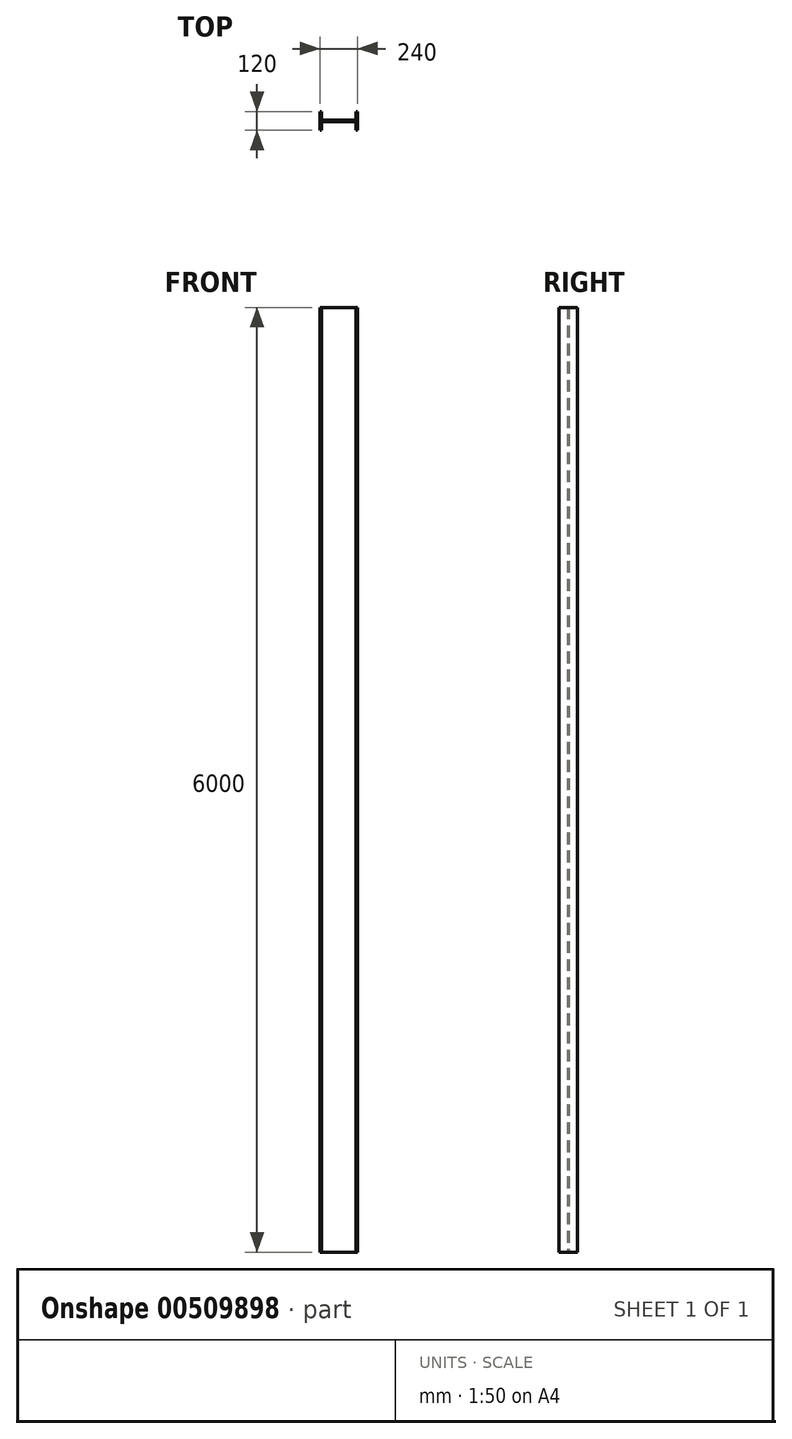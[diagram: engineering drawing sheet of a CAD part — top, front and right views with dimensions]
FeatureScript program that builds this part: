
annotation { "Feature Type Name" : "Feature", "Feature Type Description" : "" }
export const myFeature = defineFeature(function(context is Context, id is Id, definition is map)
    precondition{}
    {
        {
            var Q0;
            Q0=qCreatedBy(makeId("Top.planeOp"),FACE);
            var sketch = newSketch(context, id + "F0", { "sketchPlane" : qUnion([Q0])});
            skLineSegment(sketch, "E0", {"start": v(0, 0) * mm, "end": v(0, -120) * mm});
            skLineSegment(sketch, "E1", {"start": v(0, -120) * mm, "end": v(-10, -120) * mm});
            skLineSegment(sketch, "E2", {"start": v(-10, -120) * mm, "end": v(-10, -65) * mm});
            skLineSegment(sketch, "E3", {"start": v(-10, -65) * mm, "end": v(-230, -65) * mm});
            skLineSegment(sketch, "E4", {"start": v(-230, -65) * mm, "end": v(-230, -120) * mm});
            skLineSegment(sketch, "E5", {"start": v(-230, -120) * mm, "end": v(-240, -120) * mm});
            skLineSegment(sketch, "E6", {"start": v(-240, -120) * mm, "end": v(-240, 0) * mm});
            skLineSegment(sketch, "E7", {"start": v(-240, 0) * mm, "end": v(-230, 0) * mm});
            skLineSegment(sketch, "E8", {"start": v(-230, 0) * mm, "end": v(-230, -55) * mm});
            skLineSegment(sketch, "E9", {"start": v(-230, -55) * mm, "end": v(-10, -55) * mm});
            skLineSegment(sketch, "E10", {"start": v(-10, -55) * mm, "end": v(-10, 0) * mm});
            skLineSegment(sketch, "E11", {"start": v(-10, 0) * mm, "end": v(0, 0) * mm});
            skSolve(sketch);
        }
        {
            var Q0;
            Q0=makeQuery(id+"F0.imprint","IMPRINT",FACE,{"disambiguationData":[TD([[makeQuery(id+"F0.imprint","IMPRINT",EDGE,{"derivedFrom":sQuery(id+"F0.wireOp",EDGE,"E0")}),-1.0]])]});
            extrude(context, id + "F1", {"entities" : qUnion([Q0]), "depth" : 6000 * mm});
        }
    });
